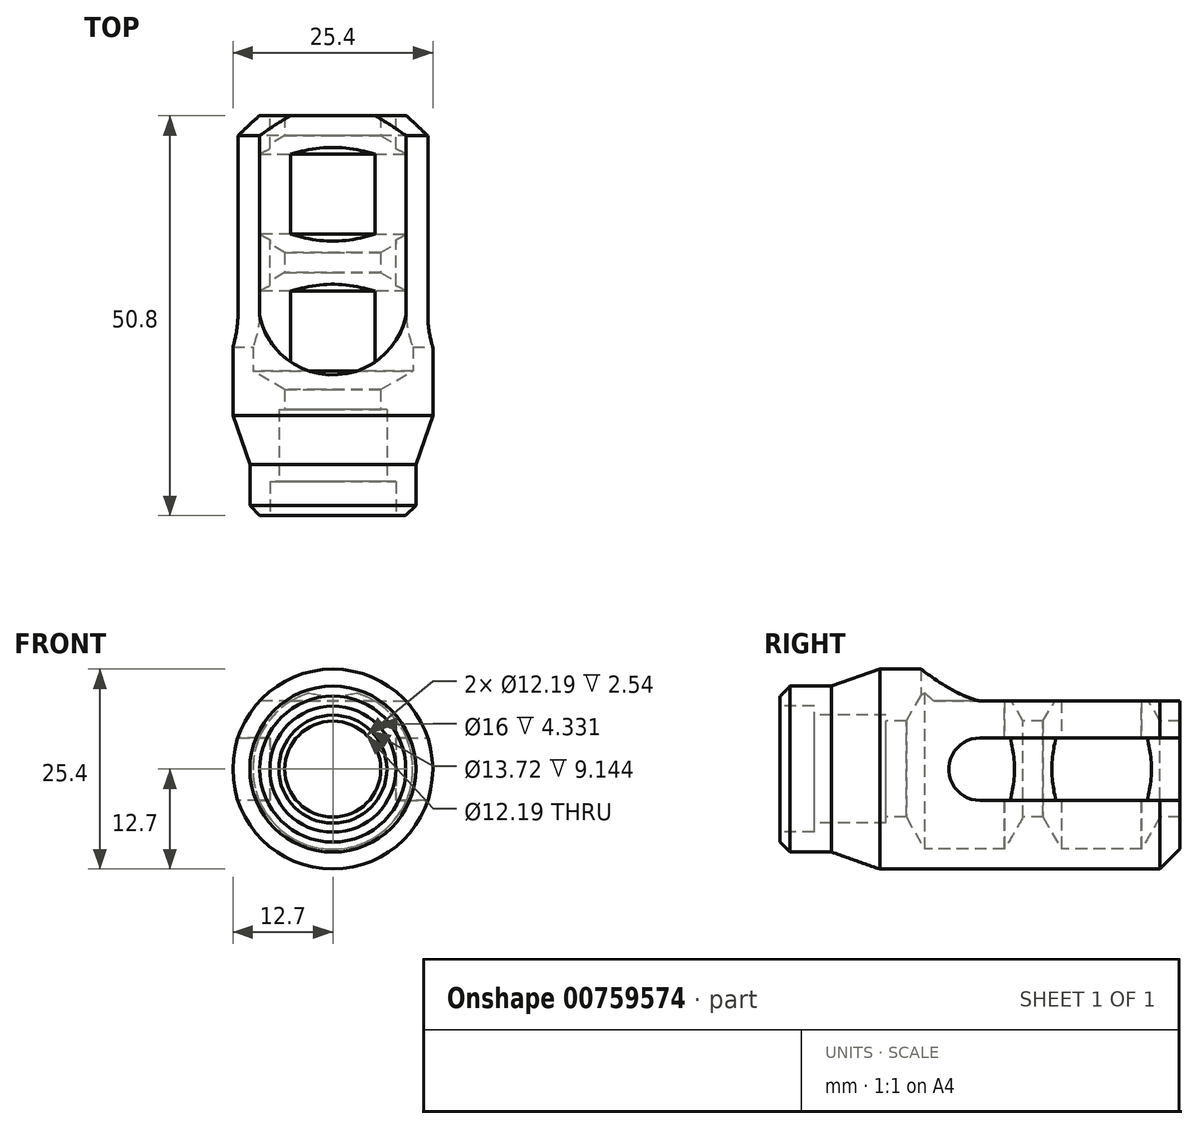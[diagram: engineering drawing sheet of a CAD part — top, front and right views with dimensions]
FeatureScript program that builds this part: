
annotation { "Feature Type Name" : "Feature", "Feature Type Description" : "" }
export const myFeature = defineFeature(function(context is Context, id is Id, definition is map)
    precondition{}
    {
        {
            var Q0;
            Q0=qCreatedBy(makeId("Top.planeOp"),FACE);
            var sketch = newSketch(context, id + "F0", { "sketchPlane" : qUnion([Q0])});
            skLineSegment(sketch, "E0", {"start": v(0, 0) * mm, "end": v(0, 130.85) * mm});
            skLineSegment(sketch, "E1", {"start": v(-10.54, 2.2) * mm, "end": v(-12.7, 8.37) * mm});
            skLineSegment(sketch, "E2", {"start": v(-12.7, 8.37) * mm, "end": v(-12.7, 46.47) * mm});
            skLineSegment(sketch, "E3", {"start": v(-12.7, 46.47) * mm, "end": v(-6.1, 46.47) * mm});
            skLineSegment(sketch, "E4", {"start": v(-6.1, 43.93) * mm, "end": v(-6.1, 43.93) * mm});
            skLineSegment(sketch, "E5", {"start": v(-6.1, 43.93) * mm, "end": v(-10.16, 41.58) * mm});
            skLineSegment(sketch, "E6", {"start": v(-10.16, 41.58) * mm, "end": v(-10.16, 31.42) * mm});
            skLineSegment(sketch, "E7", {"start": v(-10.16, 31.42) * mm, "end": v(-6.1, 29.08) * mm});
            skLineSegment(sketch, "E8", {"start": v(-6.1, 29.08) * mm, "end": v(-6.1, 29.08) * mm});
            skLineSegment(sketch, "E9", {"start": v(-6.1, 26.54) * mm, "end": v(-6.1, 26.54) * mm});
            skLineSegment(sketch, "E10", {"start": v(-6.1, 26.54) * mm, "end": v(-10.16, 24.2) * mm});
            skLineSegment(sketch, "E11", {"start": v(-10.16, 24.2) * mm, "end": v(-10.16, 14.03) * mm});
            skLineSegment(sketch, "E12", {"start": v(-10.16, 14.03) * mm, "end": v(-6.1, 11.68) * mm});
            skLineSegment(sketch, "E13", {"start": v(-6.1, 11.68) * mm, "end": v(-6.1, 11.68) * mm});
            skLineSegment(sketch, "E14", {"start": v(-6.1, 46.47) * mm, "end": v(-6.1, 43.93) * mm});
            skLineSegment(sketch, "E15", {"start": v(-6.1, 9.14) * mm, "end": v(-6.86, 9.14) * mm});
            skLineSegment(sketch, "E16", {"start": v(-6.86, 9.14) * mm, "end": v(-6.86, 0) * mm});
            skLineSegment(sketch, "E17", {"start": v(-6.86, 0) * mm, "end": v(-8, 0) * mm});
            skPoint(sketch, "E18.orphan", {"position": v(0, 11.68) * mm});
            skLineSegment(sketch, "E19.trimOffspring", {"start": v(-6.1, 11.68) * mm, "end": v(-6.1, 9.14) * mm});
            skPoint(sketch, "E20.orphan", {"position": v(0, 29.08) * mm});
            skLineSegment(sketch, "E21.trimOffspring", {"start": v(-6.1, 29.08) * mm, "end": v(-6.1, 26.54) * mm});
            skLineSegment(sketch, "E22", {"start": v(-10.54, 2.2) * mm, "end": v(-10.54, -4.33) * mm});
            skLineSegment(sketch, "E23", {"start": v(-10.54, -4.33) * mm, "end": v(-8, -4.33) * mm});
            skLineSegment(sketch, "E24", {"start": v(-8, -4.33) * mm, "end": v(-8, 0) * mm});
            skPoint(sketch, "E25.orphan", {"position": v(-9.77, 0) * mm});
            skSolve(sketch);
        }
        {
            var Q0;
            Q0 = qSketchRegion(id + "F0", true);
            var Q1;
            Q1=sQuery(id+"F0.wireOp",EDGE,"E0");
            revolve(context, id + "F1", {"surfaceOperationType" : NewSurfaceOperationType.NEW, "entities" : qUnion([Q0]), "axis" : qUnion([Q1]), "revolveType" : RevolveType.FULL});
        }
        {
            var Q0;
            Q0=makeQuery(id+"F1.opRevolve","SWEPT_FACE",FACE,{"disambiguationData":[OSD([sQuery(id+"F0.wireOp",EDGE,"E3")])]});
            var sketch = newSketch(context, id + "F2", { "sketchPlane" : qUnion([Q0])});
            skLineSegment(sketch, "E26", {"start": v(0, 0) * mm, "end": v(0, 8.64) * mm});
            skLineSegment(sketch, "E27", {"start": v(0, 8.64) * mm, "end": v(-25.4, 8.64) * mm});
            skLineSegment(sketch, "E28", {"start": v(-25.4, 8.64) * mm, "end": v(-25.4, 25.73) * mm});
            skLineSegment(sketch, "E29", {"start": v(-25.4, 25.73) * mm, "end": v(25.4, 25.73) * mm});
            skLineSegment(sketch, "E30", {"start": v(25.4, 25.73) * mm, "end": v(25.4, 8.64) * mm});
            skLineSegment(sketch, "E31", {"start": v(25.4, 8.64) * mm, "end": v(0, 8.64) * mm});
            skSolve(sketch);
        }
        {
            var Q0;
            Q0 = qSketchRegion(id + "F2", true);
            extrude(context, id + "F3", {"entities" : qUnion([Q0]), "operationType" : NewBodyOperationType.REMOVE, "oppositeDirection" : true, "depth" : 25.4 * mm, "offsetDistance" : 25.4 * mm});
        }
        {
            var Q0;
            Q0=makeQuery(id+"F1.opRevolve","SWEPT_FACE",FACE,{"disambiguationData":[OSD([sQuery(id+"F0.wireOp",EDGE,"E3")])]});
            var sketch = newSketch(context, id + "F4", { "sketchPlane" : qUnion([Q0])});
            skLineSegment(sketch, "E32.bottom", {"start": v(-8, 3.97) * mm, "end": v(-20.7, 3.97) * mm});
            skLineSegment(sketch, "E32.top", {"start": v(-8, -3.97) * mm, "end": v(-20.7, -3.97) * mm});
            skLineSegment(sketch, "E32.left", {"start": v(-8, 3.97) * mm, "end": v(-8, -3.97) * mm});
            skLineSegment(sketch, "E32.right", {"start": v(-20.7, 3.97) * mm, "end": v(-20.7, -3.97) * mm});
            skLineSegment(sketch, "E33", {"start": v(0, 0) * mm, "end": v(-8, 0) * mm});
            skLineSegment(sketch, "E34.MirrorCS", {"start": v(8, 3.97) * mm, "end": v(8, -3.97) * mm});
            skLineSegment(sketch, "E35.MirrorCS", {"start": v(8, -3.97) * mm, "end": v(20.7, -3.97) * mm});
            skLineSegment(sketch, "E36.MirrorCS", {"start": v(20.7, 3.97) * mm, "end": v(20.7, -3.97) * mm});
            skLineSegment(sketch, "E37.MirrorCS", {"start": v(8, 3.97) * mm, "end": v(20.7, 3.97) * mm});
            skSolve(sketch);
        }
        {
            var Q0;
            Q0 = qSketchRegion(id + "F4", true);
            extrude(context, id + "F5", {"entities" : qUnion([Q0]), "operationType" : NewBodyOperationType.REMOVE, "oppositeDirection" : true, "depth" : 25.4 * mm, "offsetDistance" : 25.4 * mm});
        }
        {
            var Q0;
            {var subQ0=sQuery(id+"F0.wireOp",EDGE,"E2");var subQ1=sQuery(id+"F0.wireOp",EDGE,"E3");Q0=makeQuery(id+"F5.boolean.opBoolean","SPLIT",EDGE,{"disambiguationData":[TD([makeQuery(id+"F5.opExtrude","SWEPT_FACE",FACE,{"disambiguationData":[OSD([sQuery(id+"F4.wireOp",EDGE,"E32.bottom")])]})])],"derivedFrom":makeQuery(id+"F1.opRevolve","SWEPT_EDGE",EDGE,{"disambiguationData":[OSD([subQ0,subQ1])]})});}
            var Q1;
            {var subQ0=sQuery(id+"F0.wireOp",EDGE,"E2");var subQ1=sQuery(id+"F0.wireOp",EDGE,"E3");Q1=makeQuery(id+"F5.boolean.opBoolean","SPLIT",EDGE,{"disambiguationData":[TD([makeQuery(id+"F5.opExtrude","SWEPT_FACE",FACE,{"disambiguationData":[OSD([sQuery(id+"F4.wireOp",EDGE,"E32.top")])]})])],"derivedFrom":makeQuery(id+"F1.opRevolve","SWEPT_EDGE",EDGE,{"disambiguationData":[OSD([subQ0,subQ1])]})});}
            var Q2;
            {var subQ0=sQuery(id+"F0.wireOp",EDGE,"E2");var subQ1=sQuery(id+"F0.wireOp",EDGE,"E3");Q2=makeQuery(id+"F5.boolean.opBoolean","SPLIT",EDGE,{"disambiguationData":[TD([makeQuery(id+"F5.opExtrude","SWEPT_FACE",FACE,{"disambiguationData":[OSD([sQuery(id+"F4.wireOp",EDGE,"E37.MirrorCS")])]})])],"derivedFrom":makeQuery(id+"F1.opRevolve","SWEPT_EDGE",EDGE,{"disambiguationData":[OSD([subQ0,subQ1])]})});}
            chamfer(context, id + "F6", {"entities" : qUnion([Q0, Q1, Q2]), "width" : 2.54 * mm, "tangentPropagation" : true});
        }
        {
            var Q0;
            Q0=makeQuery(id+"F3.boolean.opBoolean","COPY",FACE,{"derivedFrom":makeQuery(id+"F3.opExtrude","SWEPT_FACE",FACE,{"disambiguationData":[OSD([sQuery(id+"F2.wireOp",EDGE,"E27"),sQuery(id+"F2.wireOp",EDGE,"E31")])]})});
            var sketch = newSketch(context, id + "F7", { "sketchPlane" : qUnion([Q0])});
            skCircle(sketch, "E38", {"center": v(0, 23.07) * mm, "radius": 9.53 * mm});
            skSolve(sketch);
        }
        {
            var Q0;
            Q0 = qSketchRegion(id + "F7", true);
            extrude(context, id + "F8", {"entities" : qUnion([Q0]), "operationType" : NewBodyOperationType.REMOVE, "depth" : 25.4 * mm, "offsetDistance" : 25.4 * mm});
        }
        {
            var Q0;
            Q0=makeQuery(id+"F1.opRevolve","SWEPT_EDGE",EDGE,{"disambiguationData":[OSD([sQuery(id+"F0.wireOp",EDGE,"E22"),sQuery(id+"F0.wireOp",EDGE,"E23")])]});
            chamfer(context, id + "F9", {"entities" : qUnion([Q0]), "width" : 1.27 * mm, "tangentPropagation" : true});
        }
        {
            var Q0;
            Q0=makeQuery(id+"F5.boolean.opBoolean","COPY",FACE,{"disambiguationData":[TD([makeQuery(id+"F1.opRevolve","SWEPT_FACE",FACE,{"disambiguationData":[OSD([sQuery(id+"F0.wireOp",EDGE,"E7")])]})])],"derivedFrom":makeQuery(id+"F5.opExtrude","SWEPT_FACE",FACE,{"disambiguationData":[OSD([sQuery(id+"F4.wireOp",EDGE,"E32.left")])]})});
            var sketch = newSketch(context, id + "F10", { "sketchPlane" : qUnion([Q0])});
            skCircle(sketch, "E39", {"center": v(21.07, 0) * mm, "radius": 3.97 * mm});
            skSolve(sketch);
        }
        {
            var Q0;
            Q0 = qSketchRegion(id + "F10", true);
            extrude(context, id + "F11", {"entities" : qUnion([Q0]), "operationType" : NewBodyOperationType.REMOVE, "endBound" : BoundingType.SYMMETRIC, "oppositeDirection" : true, "depth" : 50.8 * mm, "offsetDistance" : 25.4 * mm});
        }
    });
